FCSTD DOCUMENT  (FreeCAD 0.20R29177 +426 (Git))
Label: 097_task1
License: All rights reserved
LicenseURL: http://en.wikipedia.org/wiki/All_rights_reserved
objects: TechDraw::DrawViewDimension×13, TechDraw::DrawViewDimExtent×2, Sketcher::SketchObject×1, TechDraw::DrawSVGTemplate×1, TechDraw::DrawViewPart×1, TechDraw::DrawViewAnnotation×1, TechDraw::DrawPage×1
note: 1 computed .brp shape members not serialized (recipe doc carries the construction recipe); baked Part::Feature solids carry a one-line shape summary decoded from their .brp

FEATURE [Sketcher::SketchObject] Sketch
  FullyConstrained = false
  sketch-geometry (59):
    g0: GeomPoint X=-87.7191 Y=-54.7163 Z=0
    g1: LineSegment StartX=-26.6145 StartY=-59.1149 StartZ=0 EndX=23.3855 EndY=-59.1149 EndZ=0
    g2: ArcOfCircle CenterX=23.3855 CenterY=-59.1149 CenterZ=0 NormalX=0 NormalY=0 NormalZ=1 AngleXU=0 Radius=10 StartAngle=3.92467 EndAngle=7.13953
    g3: Circle CenterX=-26.6145 CenterY=-59.1149 CenterZ=0 NormalX=0 NormalY=0 NormalZ=1 AngleXU=0 Radius=10
    g4: Circle CenterX=-140.688 CenterY=-41.9107 CenterZ=0 NormalX=0 NormalY=0 NormalZ=1 AngleXU=0 Radius=0
    g5: Ellipse CenterX=161.442 CenterY=0 CenterZ=0 NormalX=0 NormalY=0 NormalZ=1 MajorRadius=60.0002 MinorRadius=40.0001 AngleXU=0.00236889
    g6: LineSegment StartX=221.442 StartY=0.142134 StartZ=0 EndX=101.442 EndY=-0.142134 EndZ=0
    g7: LineSegment StartX=161.347 StartY=40 StartZ=0 EndX=161.537 EndY=-40 EndZ=0
    g8: GeomPoint X=206.163 Y=0.10594 Z=0
    g9: GeomPoint X=116.721 Y=-0.10594 Z=0
    g10: LineSegment StartX=-230.174 StartY=136.616 StartZ=0 EndX=-130.174 EndY=136.616 EndZ=0
    g11: LineSegment StartX=-130.174 StartY=136.616 StartZ=0 EndX=-130.174 EndY=56.6157 EndZ=0
    g12: LineSegment StartX=-130.174 StartY=56.6157 StartZ=0 EndX=-230.174 EndY=56.6157 EndZ=0
    g13: LineSegment StartX=-230.174 StartY=56.6157 StartZ=0 EndX=-230.174 EndY=136.616 EndZ=0
    g14: LineSegment StartX=-206.096 StartY=1.1533 StartZ=0 EndX=-221.096 EndY=27.1341 EndZ=0
    g15: LineSegment StartX=-221.096 StartY=27.1341 StartZ=0 EndX=-236.096 EndY=1.1533 EndZ=0
    g16: LineSegment StartX=-236.096 StartY=1.1533 StartZ=0 EndX=-206.096 EndY=1.1533 EndZ=0
    g17: Circle CenterX=-221.096 CenterY=9.81355 CenterZ=0 NormalX=0 NormalY=0 NormalZ=1 AngleXU=0 Radius=17.3205
    g18: LineSegment StartX=-152.918 StartY=-0.059128 StartZ=0 EndX=-153.211 EndY=29.9409 EndZ=0
    g19: LineSegment StartX=-153.211 StartY=29.9409 StartZ=0 EndX=-183.211 EndY=29.6477 EndZ=0
    g20: LineSegment StartX=-183.211 StartY=29.6477 StartZ=0 EndX=-182.918 EndY=-0.352326 EndZ=0
    g21: LineSegment StartX=-182.918 StartY=-0.352326 StartZ=0 EndX=-152.918 EndY=-0.059128 EndZ=0
    g22: Circle CenterX=-168.065 CenterY=14.7943 CenterZ=0 NormalX=0 NormalY=0 NormalZ=1 AngleXU=0 Radius=21.2142
    g23: LineSegment StartX=-94.7205 StartY=0.690742 StartZ=0 EndX=-85.4755 EndY=29.2307 EndZ=0
    g24: LineSegment StartX=-85.4755 StartY=29.2307 StartZ=0 EndX=-109.762 EndY=46.8426 EndZ=0
    g25: LineSegment StartX=-109.762 StartY=46.8426 StartZ=0 EndX=-134.017 EndY=29.1874 EndZ=0
    g26: LineSegment StartX=-134.017 StartY=29.1874 StartZ=0 EndX=-124.721 EndY=0.663951 EndZ=0
    g27: LineSegment StartX=-124.721 StartY=0.663951 StartZ=0 EndX=-94.7205 EndY=0.690742 EndZ=0
    g28: Circle CenterX=-109.739 CenterY=21.3231 CenterZ=0 NormalX=0 NormalY=0 NormalZ=1 AngleXU=0 Radius=25.5195
    g29: LineSegment StartX=-26.1571 StartY=0.886743 StartZ=0 EndX=-11.2296 EndY=26.9094 EndZ=0
    g30: LineSegment StartX=-11.2296 StartY=26.9094 StartZ=0 EndX=-26.3021 EndY=52.8483 EndZ=0
    g31: LineSegment StartX=-26.3021 StartY=52.8483 StartZ=0 EndX=-56.3021 EndY=52.7645 EndZ=0
    g32: LineSegment StartX=-56.3021 StartY=52.7645 StartZ=0 EndX=-71.2296 EndY=26.7419 EndZ=0
    g33: LineSegment StartX=-71.2296 StartY=26.7419 StartZ=0 EndX=-56.1571 EndY=0.803014 EndZ=0
    g34: LineSegment StartX=-56.1571 StartY=0.803014 StartZ=0 EndX=-26.1571 EndY=0.886743 EndZ=0
    g35: Circle CenterX=-41.2296 CenterY=26.8256 CenterZ=0 NormalX=0 NormalY=0 NormalZ=1 AngleXU=0 Radius=30.0001
    g36: LineSegment StartX=50.2533 StartY=1.52116 StartZ=0 EndX=68.8633 EndY=25.0516 EndZ=0
    g37: LineSegment StartX=68.8633 StartY=25.0516 StartZ=0 EndX=62.0696 EndY=54.2725 EndZ=0
    g38: LineSegment StartX=62.0696 StartY=54.2725 StartZ=0 EndX=34.988 EndY=67.1799 EndZ=0
    g39: LineSegment StartX=34.988 StartY=67.1799 StartZ=0 EndX=8.01149 EndY=54.0543 EndZ=0
    g40: LineSegment StartX=8.01149 StartY=54.0543 StartZ=0 EndX=1.45394 EndY=24.7795 EndZ=0
    g41: LineSegment StartX=1.45394 StartY=24.7795 StartZ=0 EndX=20.2533 EndY=1.40005 EndZ=0
    g42: LineSegment StartX=20.2533 StartY=1.40005 StartZ=0 EndX=50.2533 EndY=1.52116 EndZ=0
    g43: Circle CenterX=35.1276 CenterY=32.6084 CenterZ=0 NormalX=0 NormalY=0 NormalZ=1 AngleXU=0 Radius=34.5718
    g44: ArcOfCircle CenterX=-69.1739 CenterY=107.176 CenterZ=0 NormalX=0 NormalY=0 NormalZ=1 AngleXU=0 Radius=10 StartAngle=1.5708 EndAngle=4.71239
    g45: ArcOfCircle CenterX=-54.1739 CenterY=107.176 CenterZ=0 NormalX=0 NormalY=0 NormalZ=1 AngleXU=0 Radius=10 StartAngle=4.71239 EndAngle=7.85398
    g46: LineSegment StartX=-69.1739 StartY=97.1756 StartZ=0 EndX=-54.1739 EndY=97.1756 EndZ=0
    g47: LineSegment StartX=-54.1739 StartY=117.176 StartZ=0 EndX=-69.1739 EndY=117.176 EndZ=0
    g48: GeomPoint X=15 Y=100 Z=0
    g49: LineSegment StartX=-282.046 StartY=-11.4652 StartZ=0 EndX=-252.046 EndY=-11.4652 EndZ=0
    g50: LineSegment StartX=47.6633 StartY=135.046 StartZ=0 EndX=48.107 EndY=105.046 EndZ=0
    g51: LineSegment StartX=48.107 StartY=105.046 StartZ=0 EndX=69.634 EndY=84.1466 EndZ=0
    g52: LineSegment StartX=69.634 StartY=84.1466 StartZ=0 EndX=99.634 EndY=84.5903 EndZ=0
    g53: LineSegment StartX=99.634 StartY=84.5903 StartZ=0 EndX=120.533 EndY=106.117 EndZ=0
    g54: LineSegment StartX=120.533 StartY=106.117 StartZ=0 EndX=120.09 EndY=136.117 EndZ=0
    g55: LineSegment StartX=120.09 StartY=136.117 StartZ=0 EndX=98.5627 EndY=157.017 EndZ=0
    g56: LineSegment StartX=98.5627 StartY=157.017 StartZ=0 EndX=68.5627 EndY=156.573 EndZ=0
    g57: LineSegment StartX=68.5627 StartY=156.573 StartZ=0 EndX=47.6633 EndY=135.046 EndZ=0
    g58: Circle CenterX=84.0983 CenterY=120.582 CenterZ=0 NormalX=0 NormalY=0 NormalZ=1 AngleXU=0 Radius=39.2012
  constraints (112):
    c: Horizontal(g1)
    c: DistanceX(g1,g1) = 50
    c: Coincident(g2,g1)
    c: Radius(g2) = 10
    c: Coincident(g3,g1)
    c: Radius(g3) = 10
    c: InternalAlignment(g6-g9 -> g5) x4
    c: PointOnObject(g5,g-1)
    c: DistanceY(g7,g7) = 80
    c: DistanceX(g6,g6) = 120
    c: Coincident(g10,g11)
    c: Coincident(g11,g12)
    c: Coincident(g12,g13)
    c: Coincident(g13,g10)
    c: Horizontal(g10)
    c: Horizontal(g12)
    c: Vertical(g11)
    c: Vertical(g13)
    c: DistanceX(g10,g10) = 100
    c: DistanceY(g11,g11) = 80
    c: Coincident(g14,g15)
    c: Coincident(g15,g16)
    c: Coincident(g16,g14)
    c: Equal(g14,g15)
    c: Equal(g14,g16)
    c: PointOnObject(g14,g17)
    c: PointOnObject(g15,g17)
    c: PointOnObject(g16,g17)
    c: DistanceX(g16,g16) = 30
    c: Coincident(g18,g19)
    c: Coincident(g19,g20)
    c: Coincident(g20,g21)
    c: Coincident(g21,g18)
    c: Equal(g18,g19)
    c: Equal(g18,g20)
    c: Equal(g18,g21)
    c: PointOnObject(g18,g22)
    c: PointOnObject(g19,g22)
    c: PointOnObject(g20,g22)
    c: PointOnObject(g21,g22)
    c: DistanceX(g21,g21) = 30
    c: Coincident(g23,g24)
    c: Coincident(g24,g25)
    c: Coincident(g25,g26)
    c: Coincident(g26,g27)
    c: Coincident(g27,g23)
    c: Equal(g23, g24-g27) x4
    c: PointOnObject(g23,g28)
    c: PointOnObject(g24,g28)
    c: PointOnObject(g25,g28)
    c: PointOnObject(g26,g28)
    c: PointOnObject(g27,g28)
    c: DistanceX(g27,g27) = 30
    c: Coincident(g29,g30)
    c: Coincident(g30,g31)
    c: Coincident(g31,g32)
    c: Coincident(g32,g33)
    c: Coincident(g33,g34)
    c: Coincident(g34,g29)
    c: Equal(g29, g30-g34) x5
    c: PointOnObject(g29,g35)
    c: PointOnObject(g30,g35)
    c: PointOnObject(g31,g35)
    c: PointOnObject(g32,g35)
    c: PointOnObject(g33,g35)
    c: PointOnObject(g34,g35)
    c: DistanceX(g34,g34) = 30
    c: Coincident(g36,g37)
    c: Coincident(g37,g38)
    c: Coincident(g38,g39)
    c: Coincident(g39,g40)
    c: Coincident(g40,g41)
    c: Coincident(g41,g42)
    c: Coincident(g42,g36)
    c: Equal(g36, g37-g42) x6
    c: PointOnObject(g36,g43)
    c: PointOnObject(g37,g43)
    c: PointOnObject(g38,g43)
    c: PointOnObject(g39,g43)
    c: PointOnObject(g40,g43)
    c: PointOnObject(g41,g43)
    c: PointOnObject(g42,g43)
    c: DistanceX(g42,g42) = 30
    c: Tangent(g44,g46) = -1.5708
    c: Tangent(g46,g45) = -1.5708
    c: Tangent(g45,g47) = -1.5708
    c: Tangent(g47,g44) = -1.5708
    c: Equal(g44,g45)
    c: Horizontal(g46)
    c: Radius(g45) = 10
    c: DistanceX(g46,g46) = 15
    c: DistanceX(g49,g49) = 30
    c: DistanceX(g48) = 15
    c: DistanceY(g48) = 100
    c: Coincident(g50,g51)
    c: Coincident(g51,g52)
    c: Coincident(g52,g53)
    c: Coincident(g53,g54)
    c: Coincident(g54,g55)
    c: Coincident(g55,g56)
    c: Coincident(g56,g57)
    c: Coincident(g57,g50)
    c: Equal(g50, g51-g57) x7
    c: PointOnObject(g50,g58)
    c: PointOnObject(g51,g58)
    c: PointOnObject(g52,g58)
    c: PointOnObject(g53,g58)
    c: PointOnObject(g54,g58)
    c: PointOnObject(g55,g58)
    c: PointOnObject(g56,g58)
    c: PointOnObject(g57,g58)
    c: DistanceX(g52,g52) = 30
FEATURE [TechDraw::DrawSVGTemplate] Template001
  EditableTexts = APPROVER_NAME=KEYUR SURATI; AUTHOR_NAME=YASH PATEL(228); DATE=2023-04-18; DN=7; DOCUMENT_TYPE=SKETCH; OWNER_NAME=AMTICS; SCALE=1:0.50; SHEET=7; SIZE=A4; TITLELINE-1=INTRODUCTION TO FreeCAD
  Height = 210
  Orientation = 1
  Width = 297
FEATURE [TechDraw::DrawViewPart] View
  CoarseView = false
  Direction = (0,0,1)
  Focus = 100
  HardHidden = false
  IsoCount = 0
  IsoHidden = false
  IsoVisible = false
  LockPosition = false
  Perspective = false
  Rotation = 0
  Scale = 0.5
  ScaleType = 0
  SeamHidden = false
  SeamVisible = true
  SmoothHidden = false
  SmoothVisible = true
  Source = -> [Sketch]
  X = 153.213
  XDirection = (1,0,0)
  Y = 127.958
FEATURE [TechDraw::DrawViewDimension] Dimension
  AngleOverride = false
  Arbitrary = false
  ArbitraryTolerances = false
  EqualTolerance = true
  ExtensionAngle = 0
  FormatSpec = %.2w
  FormatSpecOverTolerance = %+.2w
  FormatSpecUnderTolerance = %+.2w
  Inverted = false
  LineAngle = 0
  LockPosition = false
  MeasureType = 1
  OverTolerance = 0
  References2D = -> [View]
  Rotation = 0
  Scale = 0.5
  ScaleType = 0
  TheoreticalExact = false
  Type = 1
  UnderTolerance = 0
  X = -74.9363
  Y = 5.84217
FEATURE [TechDraw::DrawViewDimension] Dimension001
  AngleOverride = false
  Arbitrary = false
  ArbitraryTolerances = false
  EqualTolerance = true
  ExtensionAngle = 0
  FormatSpec = %.2w
  FormatSpecOverTolerance = %+.2w
  FormatSpecUnderTolerance = %+.2w
  Inverted = false
  LineAngle = 0
  LockPosition = false
  MeasureType = 1
  OverTolerance = 0
  References2D = -> [View]
  Rotation = 0
  Scale = 0.5
  ScaleType = 0
  TheoreticalExact = false
  Type = 2
  UnderTolerance = 0
  X = -108.472
  Y = 29.2565
FEATURE [TechDraw::DrawViewDimension] Dimension002
  AngleOverride = false
  Arbitrary = false
  ArbitraryTolerances = false
  EqualTolerance = true
  ExtensionAngle = 0
  FormatSpec = %.2w
  FormatSpecOverTolerance = %+.2w
  FormatSpecUnderTolerance = %+.2w
  Inverted = false
  LineAngle = 0
  LockPosition = false
  MeasureType = 1
  OverTolerance = 0
  References2D = -> [View]
  Rotation = 0
  Scale = 0.5
  ScaleType = 0
  TheoreticalExact = false
  Type = 1
  UnderTolerance = 0
  X = -95.3971
  Y = -22.4163
FEATURE [TechDraw::DrawViewDimension] Dimension003
  AngleOverride = false
  Arbitrary = false
  ArbitraryTolerances = false
  EqualTolerance = true
  ExtensionAngle = 0
  FormatSpec = %.2w
  FormatSpecOverTolerance = %+.2w
  FormatSpecUnderTolerance = %+.2w
  Inverted = false
  LineAngle = 0
  LockPosition = false
  MeasureType = 1
  OverTolerance = 0
  References2D = -> [View]
  Rotation = 0
  Scale = 0.5
  ScaleType = 0
  TheoreticalExact = false
  Type = 1
  UnderTolerance = 0
  X = -119.031
  Y = -29.3846
FEATURE [TechDraw::DrawViewDimension] Dimension004
  AngleOverride = false
  Arbitrary = false
  ArbitraryTolerances = false
  EqualTolerance = true
  ExtensionAngle = 0
  FormatSpec = %.2w
  FormatSpecOverTolerance = %+.2w
  FormatSpecUnderTolerance = %+.2w
  Inverted = false
  LineAngle = 0
  LockPosition = false
  MeasureType = 1
  OverTolerance = 0
  References2D = -> [View]
  Rotation = 0
  Scale = 0.5
  ScaleType = 0
  TheoreticalExact = false
  Type = 1
  UnderTolerance = 0
  X = -69.0279
  Y = -24.1943
FEATURE [TechDraw::DrawViewDimension] Dimension005
  AngleOverride = false
  Arbitrary = false
  ArbitraryTolerances = false
  EqualTolerance = true
  ExtensionAngle = 0
  FormatSpec = %.2w
  FormatSpecOverTolerance = %+.2w
  FormatSpecUnderTolerance = %+.2w
  Inverted = false
  LineAngle = 0
  LockPosition = false
  MeasureType = 1
  OverTolerance = 0
  References2D = -> [View]
  Rotation = 0
  Scale = 0.5
  ScaleType = 0
  TheoreticalExact = false
  Type = 1
  UnderTolerance = 0
  X = -40.1487
  Y = -24.6314
FEATURE [TechDraw::DrawViewDimension] Dimension006
  AngleOverride = false
  Arbitrary = false
  ArbitraryTolerances = false
  EqualTolerance = true
  ExtensionAngle = 0
  FormatSpec = %.2w
  FormatSpecOverTolerance = %+.2w
  FormatSpecUnderTolerance = %+.2w
  Inverted = false
  LineAngle = 0
  LockPosition = false
  MeasureType = 1
  OverTolerance = 0
  References2D = -> [View]
  Rotation = 0
  Scale = 0.5
  ScaleType = 0
  TheoreticalExact = false
  Type = 1
  UnderTolerance = 0
  X = -5.86703
  Y = -23.669
FEATURE [TechDraw::DrawViewDimension] Dimension007
  AngleOverride = false
  Arbitrary = false
  ArbitraryTolerances = false
  EqualTolerance = true
  ExtensionAngle = 0
  FormatSpec = %.2w
  FormatSpecOverTolerance = %+.2w
  FormatSpecUnderTolerance = %+.2w
  Inverted = false
  LineAngle = 0
  LockPosition = false
  MeasureType = 1
  OverTolerance = 0
  References2D = -> [View]
  Rotation = 0
  Scale = 0.5
  ScaleType = 0
  TheoreticalExact = false
  Type = 1
  UnderTolerance = 0
  X = 32.5579
  Y = -22.702
FEATURE [TechDraw::DrawViewDimension] Dimension008
  AngleOverride = false
  Arbitrary = false
  ArbitraryTolerances = false
  EqualTolerance = true
  ExtensionAngle = 0
  FormatSpec = %.2w
  FormatSpecOverTolerance = %+.2w
  FormatSpecUnderTolerance = %+.2w
  Inverted = false
  LineAngle = 0
  LockPosition = false
  MeasureType = 1
  OverTolerance = 0
  References2D = -> [View]
  Rotation = 0
  Scale = 0.5
  ScaleType = 0
  TheoreticalExact = false
  Type = 1
  UnderTolerance = 0
  X = 57.2482
  Y = 17.6535
FEATURE [TechDraw::DrawViewDimension] Dimension009
  AngleOverride = false
  Arbitrary = false
  ArbitraryTolerances = false
  EqualTolerance = true
  ExtensionAngle = 0
  FormatSpec = ⌀%.2w
  FormatSpecOverTolerance = %+.2w
  FormatSpecUnderTolerance = %+.2w
  Inverted = false
  LineAngle = 0
  LockPosition = false
  MeasureType = 1
  OverTolerance = 0
  References2D = -> [View]
  Rotation = 0
  Scale = 0.5
  ScaleType = 0
  TheoreticalExact = false
  Type = 5
  UnderTolerance = 0
  X = -12.0779
  Y = -52.2078
FEATURE [TechDraw::DrawViewDimension] Dimension010
  AngleOverride = false
  Arbitrary = false
  ArbitraryTolerances = false
  EqualTolerance = true
  ExtensionAngle = 0
  FormatSpec = R%.2w
  FormatSpecOverTolerance = %+.2w
  FormatSpecUnderTolerance = %+.2w
  Inverted = false
  LineAngle = 0
  LockPosition = false
  MeasureType = 1
  OverTolerance = 0
  References2D = -> [View]
  Rotation = 0
  Scale = 0.5
  ScaleType = 0
  TheoreticalExact = false
  Type = 4
  UnderTolerance = 0
  X = 22.2078
  Y = -41.6883
FEATURE [TechDraw::DrawViewDimension] Dimension011
  AngleOverride = false
  Arbitrary = false
  ArbitraryTolerances = false
  EqualTolerance = true
  ExtensionAngle = 0
  FormatSpec = ⌀%.2w
  FormatSpecOverTolerance = %+.2w
  FormatSpecUnderTolerance = %+.2w
  Inverted = false
  LineAngle = 0
  LockPosition = false
  MeasureType = 1
  OverTolerance = 0
  References2D = -> [View]
  Rotation = 0
  Scale = 0.5
  ScaleType = 0
  TheoreticalExact = false
  Type = 5
  UnderTolerance = 0
  X = 5.5678
  Y = 51.4531
FEATURE [TechDraw::DrawViewDimension] Dimension012
  AngleOverride = false
  Arbitrary = false
  ArbitraryTolerances = false
  EqualTolerance = true
  ExtensionAngle = 0
  FormatSpec = %.2w
  FormatSpecOverTolerance = %+.2w
  FormatSpecUnderTolerance = %+.2w
  Inverted = false
  LineAngle = 0
  LockPosition = false
  MeasureType = 1
  OverTolerance = 0
  References2D = -> [View]
  Rotation = 0
  Scale = 0.5
  ScaleType = 0
  TheoreticalExact = false
  Type = 1
  UnderTolerance = 0
  X = -16.4653
  Y = 53.2656
FEATURE [TechDraw::DrawViewAnnotation] Annotation
  Font = osifont
  LineSpace = 80
  LockPosition = false
  MaxWidth = -1
  Rotation = 0
  Scale = 0.5
  ScaleType = 0
  Text = ##: ALL DIMENSIONS ARE IN mm.
  TextSize = 5
  TextStyle = 0
  X = 186.651
  Y = 42.8353
FEATURE [TechDraw::DrawViewDimExtent] DimExtent
  AngleOverride = false
  Arbitrary = false
  ArbitraryTolerances = false
  CosmeticTags = a52b3d59-967c-4c18-a4f0-baade0d190b9 | eb71fe5c-0829-4808-ac38-6f87bea2f0d8
  DirExtent = 0
  EqualTolerance = true
  ExtensionAngle = 0
  FormatSpec = %.2w
  FormatSpecOverTolerance = %+.2w
  FormatSpecUnderTolerance = %+.2w
  Inverted = false
  LineAngle = 0
  LockPosition = false
  MeasureType = 1
  OverTolerance = 0
  References2D = -> [View]
  Rotation = 0
  Scale = 0.5
  ScaleType = 0
  Source = -> [View]
  TheoreticalExact = false
  Type = 1
  UnderTolerance = 0
  X = 95.2187
  Y = 6.95951
FEATURE [TechDraw::DrawViewDimExtent] DimExtent001
  AngleOverride = false
  Arbitrary = false
  ArbitraryTolerances = false
  CosmeticTags = 4f2716f3-cdcc-4532-b19e-201747276d52 | 8a2d14f7-0a32-4e83-a822-17acca00ffd6
  DirExtent = 1
  EqualTolerance = true
  ExtensionAngle = 0
  FormatSpec = %.2w
  FormatSpecOverTolerance = %+.2w
  FormatSpecUnderTolerance = %+.2w
  Inverted = false
  LineAngle = 0
  LockPosition = false
  MeasureType = 1
  OverTolerance = 0
  References2D = -> [View]
  Rotation = 0
  Scale = 0.5
  ScaleType = 0
  Source = -> [View]
  TheoreticalExact = false
  Type = 2
  UnderTolerance = 0
  X = 59.4722
  Y = -17.0824
FEATURE [TechDraw::DrawPage] Page001
  KeepUpdated = true
  NextBalloonIndex = 1
  ProjectionType = 0
  Scale = 0.5
  Template = -> Template001
  Views = -> [View,Dimension,Dimension001,Dimension002,Dimension003,Dimension004,Dimension005,Dimension006,Dimension007,Dimension008,Dimension009,Dimension010,Dimension011,Dimension012,Annotation,DimExtent,DimExtent001]
